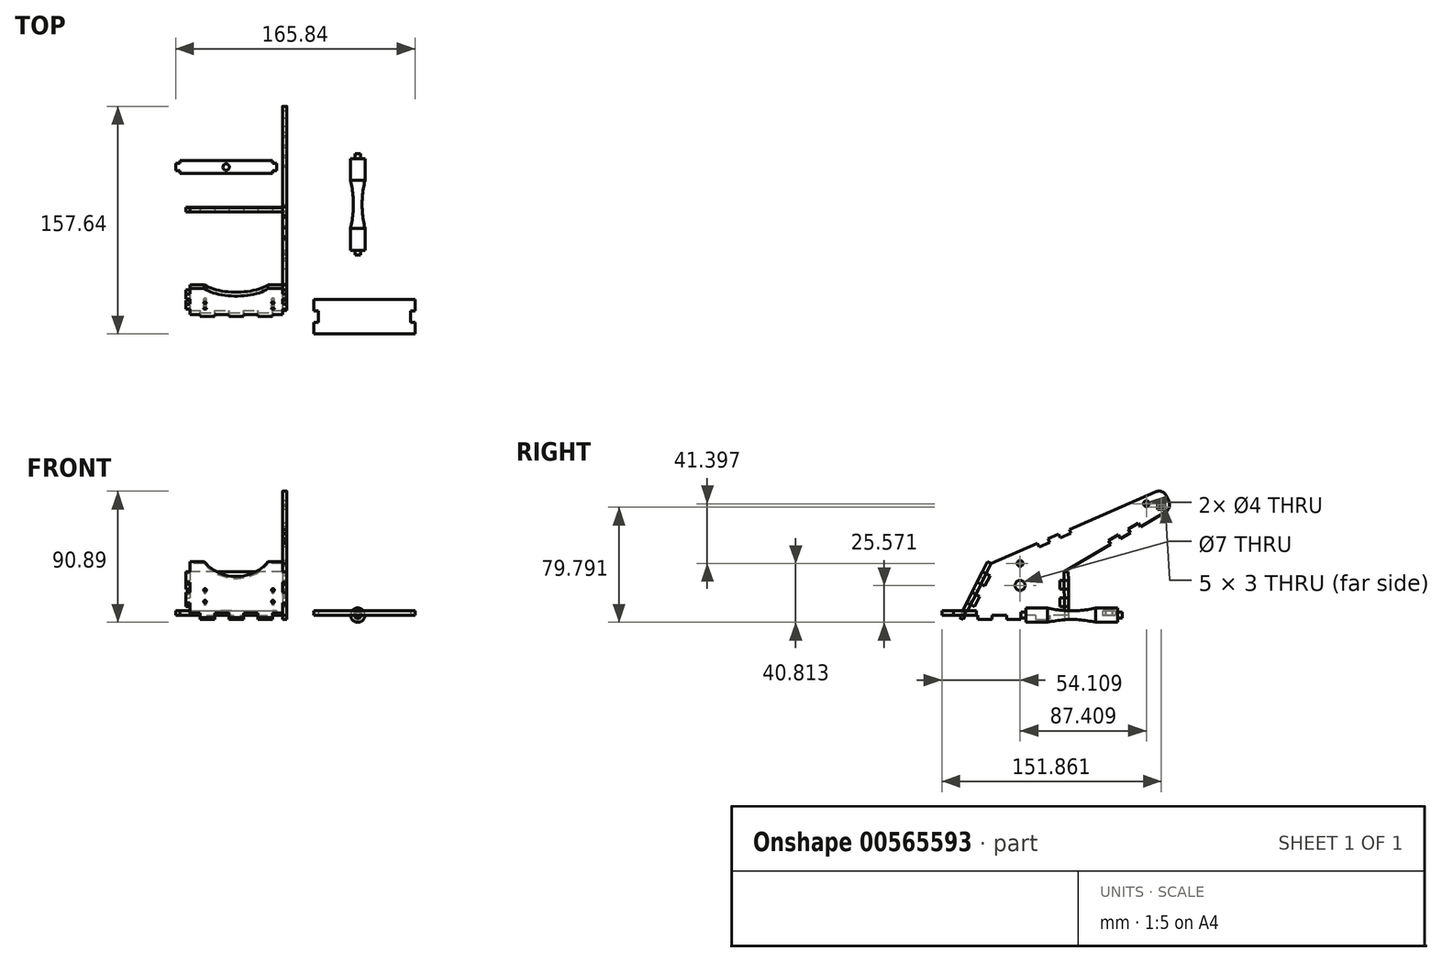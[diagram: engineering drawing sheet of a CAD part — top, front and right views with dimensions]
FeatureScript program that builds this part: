
annotation { "Feature Type Name" : "Feature", "Feature Type Description" : "" }
export const myFeature = defineFeature(function(context is Context, id is Id, definition is map)
    precondition{}
    {
        {
            var Q0;
            Q0=qCreatedBy(makeId("Right.planeOp"),FACE);
            var sketch = newSketch(context, id + "F0", { "sketchPlane" : qUnion([Q0])});
            skLineSegment(sketch, "E0", {"start": v(29.97, 0) * mm, "end": v(20, 0) * mm});
            skLineSegment(sketch, "E1", {"start": v(-38.5, 0) * mm, "end": v(-34.95, 7.16) * mm});
            skLineSegment(sketch, "E2", {"start": v(-20.7, 35.82) * mm, "end": v(11.38, 49.81) * mm});
            skLineSegment(sketch, "E3", {"start": v(100.86, 82.3) * mm, "end": v(102.33, 78.91) * mm});
            skLineSegment(sketch, "E4", {"start": v(99.88, 71.34) * mm, "end": v(82.65, 61.2) * mm});
            skLineSegment(sketch, "E5", {"start": v(29.7, 30) * mm, "end": v(29.76, 24) * mm});
            skLineSegment(sketch, "E6.top", {"start": v(-30, -3) * mm, "end": v(-20, -3) * mm});
            skLineSegment(sketch, "E6.left", {"start": v(-30, 0) * mm, "end": v(-30, -3) * mm});
            skLineSegment(sketch, "E6.right", {"start": v(-20, 0) * mm, "end": v(-20, -3) * mm});
            skLineSegment(sketch, "E7.top", {"start": v(-10, -3) * mm, "end": v(0, -3) * mm});
            skLineSegment(sketch, "E7.left", {"start": v(-10, 0) * mm, "end": v(-10, -3) * mm});
            skLineSegment(sketch, "E7.right", {"start": v(0, 0) * mm, "end": v(0, -3) * mm});
            skLineSegment(sketch, "E8.top", {"start": v(10, -3) * mm, "end": v(20, -3) * mm});
            skLineSegment(sketch, "E8.left", {"start": v(10, 0) * mm, "end": v(10, -3) * mm});
            skLineSegment(sketch, "E8.right", {"start": v(20, 0) * mm, "end": v(20, -3) * mm});
            skLineSegment(sketch, "E9.trimOffspring", {"start": v(-30, 0) * mm, "end": v(-38.5, 0) * mm});
            skLineSegment(sketch, "E10.trimOffspring", {"start": v(-10, 0) * mm, "end": v(-20, 0) * mm});
            skLineSegment(sketch, "E11.trimOffspring", {"start": v(10, 0) * mm, "end": v(0, 0) * mm});
            skPoint(sketch, "E12.visualSharp", {"position": v(98.46, 87.8) * mm});
            skArc(sketch, "E12.filletArc", {"start": v(100.86, 82.3) * mm, "mid": v(97.55, 85.48) * mm, "end": v(92.96, 85.4) * mm});
            skPoint(sketch, "E13.visualSharp", {"position": v(104.45, 74.04) * mm});
            skArc(sketch, "E13.filletArc", {"start": v(99.88, 71.34) * mm, "mid": v(102.54, 74.66) * mm, "end": v(102.33, 78.91) * mm});
            skCircle(sketch, "E14", {"center": v(86.7, 77.21) * mm, "radius": 2 * mm});
            skLineSegment(sketch, "E15", {"start": v(-36.02, 5) * mm, "end": v(-40.28, -3.57) * mm, "construction": true});
            skLineSegment(sketch, "E16", {"start": v(-30, -3) * mm, "end": v(-40, -3) * mm, "construction": true});
            skLineSegment(sketch, "E17", {"start": v(20, -3) * mm, "end": v(32.76, -3) * mm, "construction": true});
            skLineSegment(sketch, "E18", {"start": v(29.94, 3.73) * mm, "end": v(30, -3) * mm, "construction": true});
            skLineSegment(sketch, "E19", {"start": v(-35.16, 0) * mm, "end": v(-35.16, -3) * mm, "construction": true});
            skLineSegment(sketch, "E20", {"start": v(26.97, 0) * mm, "end": v(26.97, -3) * mm, "construction": true});
            skLineSegment(sketch, "E21", {"start": v(29.87, 12) * mm, "end": v(26.87, 11.97) * mm});
            skLineSegment(sketch, "E22", {"start": v(26.87, 11.97) * mm, "end": v(26.92, 5.97) * mm});
            skLineSegment(sketch, "E23", {"start": v(26.92, 5.97) * mm, "end": v(29.92, 6) * mm});
            skLineSegment(sketch, "E24", {"start": v(29.81, 18) * mm, "end": v(26.81, 17.97) * mm});
            skLineSegment(sketch, "E25", {"start": v(26.81, 17.97) * mm, "end": v(26.76, 23.97) * mm});
            skLineSegment(sketch, "E26", {"start": v(26.76, 23.97) * mm, "end": v(29.76, 24) * mm});
            skLineSegment(sketch, "E27", {"start": v(-24.26, 28.65) * mm, "end": v(-21.58, 27.32) * mm});
            skLineSegment(sketch, "E28", {"start": v(-21.58, 27.32) * mm, "end": v(-25.14, 20.16) * mm});
            skLineSegment(sketch, "E29", {"start": v(-25.14, 20.16) * mm, "end": v(-27.82, 21.5) * mm});
            skLineSegment(sketch, "E30", {"start": v(-31.39, 14.33) * mm, "end": v(-28.7, 13) * mm});
            skLineSegment(sketch, "E31", {"start": v(-28.7, 13) * mm, "end": v(-32.26, 5.83) * mm});
            skLineSegment(sketch, "E32", {"start": v(-32.26, 5.83) * mm, "end": v(-34.95, 7.16) * mm});
            skLineSegment(sketch, "E33.trimOffspring", {"start": v(-24.26, 28.65) * mm, "end": v(-20.7, 35.82) * mm});
            skLineSegment(sketch, "E34.trimOffspring", {"start": v(-31.39, 14.33) * mm, "end": v(-27.82, 21.5) * mm});
            skLineSegment(sketch, "E35.trimOffspring", {"start": v(29.92, 6) * mm, "end": v(29.97, 0) * mm});
            skLineSegment(sketch, "E36.trimOffspring", {"start": v(29.81, 18) * mm, "end": v(29.87, 12) * mm});
            skLineSegment(sketch, "E37", {"start": v(82.65, 61.2) * mm, "end": v(81.12, 63.78) * mm});
            skLineSegment(sketch, "E38", {"start": v(81.12, 63.78) * mm, "end": v(74.23, 59.71) * mm});
            skLineSegment(sketch, "E39", {"start": v(74.23, 59.71) * mm, "end": v(75.75, 57.13) * mm});
            skLineSegment(sketch, "E40", {"start": v(68.86, 53.07) * mm, "end": v(67.34, 55.65) * mm});
            skLineSegment(sketch, "E41", {"start": v(67.34, 55.65) * mm, "end": v(60.44, 51.6) * mm});
            skLineSegment(sketch, "E42", {"start": v(60.44, 51.6) * mm, "end": v(61.97, 49) * mm});
            skCircle(sketch, "E43", {"center": v(-0.7, 35.81) * mm, "radius": 2 * mm});
            skLineSegment(sketch, "E44", {"start": v(11.38, 49.81) * mm, "end": v(12.58, 47.06) * mm});
            skLineSegment(sketch, "E45", {"start": v(12.58, 47.06) * mm, "end": v(19.91, 50.26) * mm});
            skLineSegment(sketch, "E46", {"start": v(19.91, 50.26) * mm, "end": v(18.71, 53) * mm});
            skLineSegment(sketch, "E47", {"start": v(26.05, 56.2) * mm, "end": v(27.25, 53.46) * mm});
            skLineSegment(sketch, "E48", {"start": v(27.25, 53.46) * mm, "end": v(34.58, 56.66) * mm});
            skLineSegment(sketch, "E49", {"start": v(34.58, 56.66) * mm, "end": v(33.38, 59.4) * mm});
            skLineSegment(sketch, "E50.bottom", {"start": v(94.55, 76.3) * mm, "end": v(99.55, 76.3) * mm});
            skLineSegment(sketch, "E50.top", {"start": v(94.55, 73.3) * mm, "end": v(99.55, 73.3) * mm});
            skLineSegment(sketch, "E50.left", {"start": v(94.55, 76.3) * mm, "end": v(94.55, 73.3) * mm});
            skLineSegment(sketch, "E50.right", {"start": v(99.55, 76.3) * mm, "end": v(99.55, 73.3) * mm});
            skCircle(sketch, "E51", {"center": v(-0.7, 20.57) * mm, "radius": 3.5 * mm});
            skLineSegment(sketch, "E52.trimOffspring", {"start": v(18.71, 53) * mm, "end": v(26.05, 56.2) * mm});
            skLineSegment(sketch, "E53.trimOffspring", {"start": v(33.38, 59.4) * mm, "end": v(92.96, 85.4) * mm});
            skLineSegment(sketch, "E54.trimOffspring", {"start": v(61.97, 49) * mm, "end": v(29.7, 30) * mm});
            skLineSegment(sketch, "E55.trimOffspring", {"start": v(75.75, 57.13) * mm, "end": v(68.86, 53.07) * mm});
            skSolve(sketch);
        }
        {
            var Q0;
            Q0 = qSketchRegion(id + "F0", true);
            extrude(context, id + "F1", {"entities" : qUnion([Q0]), "depth" : 3 * mm, "offsetDistance" : 25 * mm});
        }
        {
            var Q0;
            Q0=makeQuery(id+"F1.opExtrude","SWEPT_FACE",FACE,{"disambiguationData":[OSD([sQuery(id+"F0.wireOp",EDGE,"E33.trimOffspring")])]});
            var sketch = newSketch(context, id + "F2", { "sketchPlane" : qUnion([Q0])});
            skLineSegment(sketch, "E56", {"start": v(3, 22.86) * mm, "end": v(-10, 22.86) * mm});
            skLineSegment(sketch, "E57", {"start": v(-67, 14.86) * mm, "end": v(-67, 6.86) * mm});
            skLineSegment(sketch, "E58", {"start": v(-64, -17.14) * mm, "end": v(-57, -17.14) * mm});
            skLineSegment(sketch, "E59", {"start": v(3, -9.14) * mm, "end": v(3, -1.14) * mm});
            skPoint(sketch, "E60", {"position": v(-32, 22.86) * mm});
            skPoint(sketch, "E61", {"position": v(-32, -17.14) * mm});
            skLineSegment(sketch, "E62", {"start": v(3, -9.14) * mm, "end": v(0, -9.14) * mm});
            skLineSegment(sketch, "E63", {"start": v(0, -9.14) * mm, "end": v(0, -17.14) * mm});
            skLineSegment(sketch, "E64", {"start": v(3, -1.14) * mm, "end": v(0, -1.14) * mm});
            skLineSegment(sketch, "E65", {"start": v(0, -1.14) * mm, "end": v(0, 6.86) * mm});
            skLineSegment(sketch, "E66", {"start": v(0, 6.86) * mm, "end": v(3, 6.86) * mm});
            skLineSegment(sketch, "E67", {"start": v(3, 22.86) * mm, "end": v(0, 22.86) * mm});
            skLineSegment(sketch, "E68", {"start": v(0, 22.86) * mm, "end": v(0, 14.86) * mm});
            skLineSegment(sketch, "E69", {"start": v(0, 14.86) * mm, "end": v(3, 14.86) * mm});
            skLineSegment(sketch, "E70", {"start": v(-67, 22.86) * mm, "end": v(-64, 22.86) * mm});
            skLineSegment(sketch, "E71", {"start": v(-64, 22.86) * mm, "end": v(-64, 14.86) * mm});
            skLineSegment(sketch, "E72", {"start": v(-64, 14.86) * mm, "end": v(-67, 14.86) * mm});
            skLineSegment(sketch, "E73", {"start": v(-67, 6.86) * mm, "end": v(-64, 6.86) * mm});
            skLineSegment(sketch, "E74", {"start": v(-64, 6.86) * mm, "end": v(-64, -1.14) * mm});
            skLineSegment(sketch, "E75", {"start": v(-64, -1.14) * mm, "end": v(-67, -1.14) * mm});
            skLineSegment(sketch, "E76", {"start": v(-67, -9.14) * mm, "end": v(-64, -9.14) * mm});
            skLineSegment(sketch, "E77", {"start": v(-64, -9.14) * mm, "end": v(-64, -17.14) * mm});
            skLineSegment(sketch, "E78.trimOffspring", {"start": v(-67, -1.14) * mm, "end": v(-67, -9.14) * mm});
            skPoint(sketch, "E79.orphan", {"position": v(-67, -17.14) * mm});
            skPoint(sketch, "E80.orphan", {"position": v(3, -17.14) * mm});
            skLineSegment(sketch, "E81.trimOffspring", {"start": v(3, 6.86) * mm, "end": v(3, 14.86) * mm});
            skLineSegment(sketch, "E82", {"start": v(0, 21.11) * mm, "end": v(0, 23.97) * mm});
            skLineSegment(sketch, "E83", {"start": v(-64, 19.7) * mm, "end": v(-64, 23.61) * mm});
            skLineSegment(sketch, "E84.top", {"start": v(-57, -20.44) * mm, "end": v(-47, -20.44) * mm});
            skLineSegment(sketch, "E84.left", {"start": v(-57, -17.14) * mm, "end": v(-57, -20.44) * mm});
            skLineSegment(sketch, "E84.right", {"start": v(-47, -17.14) * mm, "end": v(-47, -20.44) * mm});
            skPoint(sketch, "E85.oppositeSnap0", {"position": v(-52, -20.44) * mm});
            skLineSegment(sketch, "E85.top", {"start": v(-37, -20.44) * mm, "end": v(-27, -20.44) * mm});
            skLineSegment(sketch, "E85.left", {"start": v(-37, -17.14) * mm, "end": v(-37, -20.44) * mm});
            skLineSegment(sketch, "E85.right", {"start": v(-27, -17.14) * mm, "end": v(-27, -20.44) * mm});
            skLineSegment(sketch, "E86.top", {"start": v(-17, -20.44) * mm, "end": v(-7, -20.44) * mm});
            skLineSegment(sketch, "E86.left", {"start": v(-17, -17.14) * mm, "end": v(-17, -20.44) * mm});
            skLineSegment(sketch, "E86.right", {"start": v(-7, -17.14) * mm, "end": v(-7, -20.44) * mm});
            skLineSegment(sketch, "E87.trimOffspring", {"start": v(-47, -17.14) * mm, "end": v(-37, -17.14) * mm});
            skLineSegment(sketch, "E88.trimOffspring", {"start": v(-27, -17.14) * mm, "end": v(-17, -17.14) * mm});
            skLineSegment(sketch, "E89.trimOffspring", {"start": v(-7, -17.14) * mm, "end": v(0, -17.14) * mm});
            skArc(sketch, "E90", {"start": v(-54, 22.86) * mm, "mid": v(-32, 11.23) * mm, "end": v(-10, 22.86) * mm});
            skCircle(sketch, "E91", {"center": v(-53.6, 0.86) * mm, "radius": 1 * mm});
            skCircle(sketch, "E92", {"center": v(-6.6, 0.86) * mm, "radius": 1 * mm});
            skCircle(sketch, "E93", {"center": v(-53.6, -8.14) * mm, "radius": 1 * mm});
            skCircle(sketch, "E94", {"center": v(-6.6, -8.14) * mm, "radius": 1 * mm});
            skLineSegment(sketch, "E95.trimOffspring", {"start": v(-54, 22.86) * mm, "end": v(-67, 22.86) * mm});
            skSolve(sketch);
        }
        {
            var Q0;
            Q0=makeQuery(id+"F2.imprint","IMPRINT",FACE,{"disambiguationData":[TD([[makeQuery(id+"F2.imprint","IMPRINT",EDGE,{"derivedFrom":sQuery(id+"F2.wireOp",EDGE,"E57")}),1.0]])]});
            var Q1;
            {var subQ0=sQuery(id+"F2.wireOp",EDGE,"E82");var subQ1=makeQuery(id+"F2.imprint","INTERSECT",VERTEX,{"derivedFrom":[sQuery(id+"F2.wireOp",EDGE,"E67"),subQ0]});Q1=makeQuery(id+"F2.imprint","IMPRINT",FACE,{"disambiguationData":[TD([[makeQuery(id+"F2.imprint","IMPRINT",EDGE,{"disambiguationData":[TD([[subQ1,1.0]])],"derivedFrom":subQ0}),1.0]])]});}
            extrude(context, id + "F3", {"entities" : qUnion([Q0, Q1]), "depth" : 3 * mm, "offsetDistance" : 25 * mm});
        }
        {
            var Q0;
            Q0=makeQuery(id+"F1.opExtrude","SWEPT_FACE",FACE,{"disambiguationData":[OSD([sQuery(id+"F0.wireOp",EDGE,"E5")])]});
            var sketch = newSketch(context, id + "F4", { "sketchPlane" : qUnion([Q0])});
            skLineSegment(sketch, "E96.bottom", {"start": v(0, 29.73) * mm, "end": v(64, 29.73) * mm});
            skLineSegment(sketch, "E96.top", {"start": v(0, -0.27) * mm, "end": v(7, -0.27) * mm});
            skLineSegment(sketch, "E96.left", {"start": v(-3, 23.73) * mm, "end": v(-3, 17.73) * mm});
            skLineSegment(sketch, "E96.right", {"start": v(67, 23.73) * mm, "end": v(67, 17.73) * mm});
            skLineSegment(sketch, "E97.bottom", {"start": v(0, 23.73) * mm, "end": v(-3, 23.73) * mm});
            skLineSegment(sketch, "E97.left", {"start": v(0, 23.73) * mm, "end": v(0, 29.73) * mm});
            skLineSegment(sketch, "E98.bottom", {"start": v(0, 17.73) * mm, "end": v(-3, 17.73) * mm});
            skLineSegment(sketch, "E98.top", {"start": v(0, 11.73) * mm, "end": v(-3, 11.73) * mm});
            skLineSegment(sketch, "E98.left", {"start": v(0, 17.73) * mm, "end": v(0, 11.73) * mm});
            skLineSegment(sketch, "E99.bottom", {"start": v(0, 5.73) * mm, "end": v(-3, 5.73) * mm});
            skLineSegment(sketch, "E99.left", {"start": v(0, 5.73) * mm, "end": v(0, -0.27) * mm});
            skLineSegment(sketch, "E100.trimOffspring", {"start": v(-3, 11.73) * mm, "end": v(-3, 5.73) * mm});
            skLineSegment(sketch, "E101.bottom", {"start": v(67, 17.73) * mm, "end": v(64, 17.73) * mm});
            skLineSegment(sketch, "E101.top", {"start": v(67, 11.73) * mm, "end": v(64, 11.73) * mm});
            skLineSegment(sketch, "E101.right", {"start": v(64, 17.73) * mm, "end": v(64, 11.73) * mm});
            skLineSegment(sketch, "E102.top", {"start": v(67, 5.73) * mm, "end": v(64, 5.73) * mm});
            skLineSegment(sketch, "E102.right", {"start": v(64, -0.27) * mm, "end": v(64, 5.73) * mm});
            skLineSegment(sketch, "E103.top", {"start": v(67, 23.73) * mm, "end": v(64, 23.73) * mm});
            skLineSegment(sketch, "E103.right", {"start": v(64, 29.73) * mm, "end": v(64, 23.73) * mm});
            skLineSegment(sketch, "E104.trimOffspring", {"start": v(67, 11.73) * mm, "end": v(67, 5.73) * mm});
            skLineSegment(sketch, "E105.top", {"start": v(7, -3.32) * mm, "end": v(17, -3.32) * mm});
            skLineSegment(sketch, "E105.left", {"start": v(7, -0.27) * mm, "end": v(7, -3.32) * mm});
            skLineSegment(sketch, "E105.right", {"start": v(17, -0.27) * mm, "end": v(17, -3.32) * mm});
            skLineSegment(sketch, "E106.bottom", {"start": v(27, -3.32) * mm, "end": v(37, -3.32) * mm});
            skLineSegment(sketch, "E106.left", {"start": v(27, -3.32) * mm, "end": v(27, -0.27) * mm});
            skLineSegment(sketch, "E106.right", {"start": v(37, -3.32) * mm, "end": v(37, -0.27) * mm});
            skLineSegment(sketch, "E107.bottom", {"start": v(47, -3.32) * mm, "end": v(57, -3.32) * mm});
            skLineSegment(sketch, "E107.left", {"start": v(47, -3.32) * mm, "end": v(47, -0.27) * mm});
            skLineSegment(sketch, "E107.right", {"start": v(57, -3.32) * mm, "end": v(57, -0.27) * mm});
            skLineSegment(sketch, "E108.trimOffspring", {"start": v(57, -0.27) * mm, "end": v(64, -0.27) * mm});
            skLineSegment(sketch, "E109.trimOffspring", {"start": v(37, -0.27) * mm, "end": v(47, -0.27) * mm});
            skLineSegment(sketch, "E110.trimOffspring", {"start": v(17, -0.27) * mm, "end": v(27, -0.27) * mm});
            skSolve(sketch);
        }
        {
            var Q0;
            Q0 = qSketchRegion(id + "F4", true);
            extrude(context, id + "F5", {"entities" : qUnion([Q0]), "depth" : 3 * mm, "offsetDistance" : 25 * mm});
        }
        {
            var Q0;
            Q0=qCreatedBy(makeId("Top.planeOp"),FACE);
            var sketch = newSketch(context, id + "F6", { "sketchPlane" : qUnion([Q0])});
            skLineSegment(sketch, "E111", {"start": v(52.14, 0) * mm, "end": v(52.14, 70) * mm});
            skLineSegment(sketch, "E112", {"start": v(52.14, 70) * mm, "end": v(50.14, 70) * mm});
            skLineSegment(sketch, "E113", {"start": v(50.14, 70) * mm, "end": v(50.14, 66.75) * mm});
            skLineSegment(sketch, "E114", {"start": v(52.14, 0) * mm, "end": v(50.14, 0) * mm});
            skLineSegment(sketch, "E115", {"start": v(50.14, 0) * mm, "end": v(50.14, 3.25) * mm});
            skLineSegment(sketch, "E116", {"start": v(50.14, 3.25) * mm, "end": v(47.14, 3.25) * mm});
            skLineSegment(sketch, "E117", {"start": v(47.14, 3.25) * mm, "end": v(47.14, 66.75) * mm});
            skLineSegment(sketch, "E118", {"start": v(47.14, 66.75) * mm, "end": v(50.14, 66.75) * mm});
            skCircle(sketch, "E119", {"center": v(-20.86, 35) * mm, "radius": 70 * mm});
            skPoint(sketch, "E120", {"position": v(52.14, 35) * mm});
            skSolve(sketch);
        }
        {
            var Q0;
            Q0=makeQuery(id+"F6.imprint","IMPRINT",FACE,{"disambiguationData":[TD([[makeQuery(id+"F6.imprint","IMPRINT",EDGE,{"derivedFrom":sQuery(id+"F6.wireOp",EDGE,"E111")}),1.0]])]});
            var Q1;
            Q1=sQuery(id+"F6.wireOp",EDGE,"E111");
            revolve(context, id + "F7", {"surfaceOperationType" : NewSurfaceOperationType.NEW, "entities" : qUnion([Q0]), "axis" : qUnion([Q1]), "revolveType" : RevolveType.FULL});
        }
        {
            var Q0;
            Q0=qCreatedBy(makeId("Top.planeOp"),FACE);
            var sketch = newSketch(context, id + "F8", { "sketchPlane" : qUnion([Q0])});
            skLineSegment(sketch, "E121.bottom", {"start": v(-4, 63.36) * mm, "end": v(-74, 63.36) * mm});
            skLineSegment(sketch, "E121.top", {"start": v(-4, 58.36) * mm, "end": v(-74, 58.36) * mm});
            skLineSegment(sketch, "E121.left", {"start": v(-4, 63.36) * mm, "end": v(-4, 58.36) * mm});
            skLineSegment(sketch, "E121.right", {"start": v(-74, 63.36) * mm, "end": v(-74, 58.36) * mm});
            skLineSegment(sketch, "E122.bottom", {"start": v(-71, 56.36) * mm, "end": v(-7, 56.36) * mm});
            skLineSegment(sketch, "E122.top", {"start": v(-71, 65.36) * mm, "end": v(-7, 65.36) * mm});
            skLineSegment(sketch, "E122.left", {"start": v(-71, 56.36) * mm, "end": v(-71, 65.36) * mm});
            skLineSegment(sketch, "E122.right", {"start": v(-7, 56.36) * mm, "end": v(-7, 65.36) * mm});
            skCircle(sketch, "E123", {"center": v(-39, 60.86) * mm, "radius": 2.25 * mm});
            skPoint(sketch, "E123.centerSnap0", {"position": v(-39, 63.36) * mm});
            skPoint(sketch, "E123.centerSnap1", {"position": v(-7, 60.86) * mm});
            skSolve(sketch);
        }
        {
            var Q0;
            {var subQ0=sQuery(id+"F8.wireOp",EDGE,"E121.left");Q0=makeQuery(id+"F8.imprint","IMPRINT",FACE,{"disambiguationData":[TD([[makeQuery(id+"F8.imprint","IMPRINT",EDGE,{"derivedFrom":subQ0}),-1.0]])]});}
            var Q1;
            {var subQ0=sQuery(id+"F8.wireOp",EDGE,"E121.right");Q1=makeQuery(id+"F8.imprint","IMPRINT",FACE,{"disambiguationData":[TD([[makeQuery(id+"F8.imprint","IMPRINT",EDGE,{"derivedFrom":subQ0}),1.0]])]});}
            var Q2;
            {var subQ1=sQuery(id+"F8.wireOp",EDGE,"E122.bottom");Q2=makeQuery(id+"F8.imprint","IMPRINT",FACE,{"disambiguationData":[TD([[makeQuery(id+"F8.imprint","IMPRINT",EDGE,{"derivedFrom":subQ1}),1.0]])]});}
            var Q3;
            {var subQ0=sQuery(id+"F8.wireOp",EDGE,"E122.right");var subQ1=sQuery(id+"F8.wireOp",EDGE,"E121.bottom");var subQ2=makeQuery(id+"F8.imprint","INTERSECT",VERTEX,{"derivedFrom":[subQ1,subQ0]});Q3=makeQuery(id+"F8.imprint","IMPRINT",FACE,{"disambiguationData":[TD([[makeQuery(id+"F8.imprint","IMPRINT",EDGE,{"disambiguationData":[TD([[subQ2,-1.0]])],"derivedFrom":subQ1}),1.0]])]});}
            var Q4;
            {var subQ0=sQuery(id+"F8.wireOp",EDGE,"E122.left");var subQ1=sQuery(id+"F8.wireOp",EDGE,"E121.bottom");var subQ2=makeQuery(id+"F8.imprint","INTERSECT",VERTEX,{"derivedFrom":[subQ1,subQ0]});Q4=makeQuery(id+"F8.imprint","IMPRINT",FACE,{"disambiguationData":[TD([[makeQuery(id+"F8.imprint","IMPRINT",EDGE,{"disambiguationData":[TD([[subQ2,1.0]])],"derivedFrom":subQ1}),1.0]])]});}
            var Q5;
            {var subQ1=sQuery(id+"F8.wireOp",EDGE,"E122.top");Q5=makeQuery(id+"F8.imprint","IMPRINT",FACE,{"disambiguationData":[TD([[makeQuery(id+"F8.imprint","IMPRINT",EDGE,{"derivedFrom":subQ1}),-1.0]])]});}
            extrude(context, id + "F9", {"entities" : qUnion([Q0, Q1, Q2, Q3, Q4, Q5]), "depth" : 3 * mm, "offsetDistance" : 25 * mm});
        }
        {
            var Q0;
            Q0=makeQuery(id+"F9.opExtrude","CAP_EDGE",EDGE,{"disambiguationData":[OSD([sQuery(id+"F8.wireOp",EDGE,"E123")])],"isStart":false});
            var Q1;
            Q1=makeQuery(id+"F9.opExtrude","CAP_EDGE",EDGE,{"disambiguationData":[OSD([sQuery(id+"F8.wireOp",EDGE,"E123")])],"isStart":true});
            fillet(context, id + "F10", {"entities" : qUnion([Q0, Q1]), "radius" : 1.5 * mm, "tangentPropagation" : true, "allowEdgeOverflow" : false});
        }
        {
            var Q0;
            Q0=qCreatedBy(makeId("Top.planeOp"),FACE);
            var sketch = newSketch(context, id + "F11", { "sketchPlane" : qUnion([Q0])});
            skLineSegment(sketch, "E124.bottom", {"start": v(91.83, -30.81) * mm, "end": v(21.83, -30.81) * mm});
            skLineSegment(sketch, "E124.top", {"start": v(91.83, -54.81) * mm, "end": v(21.83, -54.81) * mm});
            skLineSegment(sketch, "E124.left", {"start": v(91.83, -30.81) * mm, "end": v(91.83, -38.81) * mm});
            skLineSegment(sketch, "E124.right", {"start": v(21.83, -30.81) * mm, "end": v(21.83, -38.81) * mm});
            skLineSegment(sketch, "E125.bottom", {"start": v(91.83, -38.81) * mm, "end": v(88.83, -38.81) * mm});
            skLineSegment(sketch, "E125.top", {"start": v(91.83, -46.81) * mm, "end": v(88.83, -46.81) * mm});
            skLineSegment(sketch, "E125.right", {"start": v(88.83, -38.81) * mm, "end": v(88.83, -46.81) * mm});
            skLineSegment(sketch, "E126.bottom", {"start": v(21.83, -38.81) * mm, "end": v(24.83, -38.81) * mm});
            skLineSegment(sketch, "E126.top", {"start": v(21.83, -46.81) * mm, "end": v(24.83, -46.81) * mm});
            skLineSegment(sketch, "E126.right", {"start": v(24.83, -38.81) * mm, "end": v(24.83, -46.81) * mm});
            skLineSegment(sketch, "E127.trimOffspring", {"start": v(91.83, -46.81) * mm, "end": v(91.83, -54.81) * mm});
            skLineSegment(sketch, "E128.trimOffspring", {"start": v(21.83, -46.81) * mm, "end": v(21.83, -54.81) * mm});
            skSolve(sketch);
        }
        {
            var Q0;
            Q0 = qSketchRegion(id + "F11", true);
            extrude(context, id + "F12", {"entities" : qUnion([Q0]), "depth" : 3 * mm, "offsetDistance" : 25 * mm});
        }
    });
